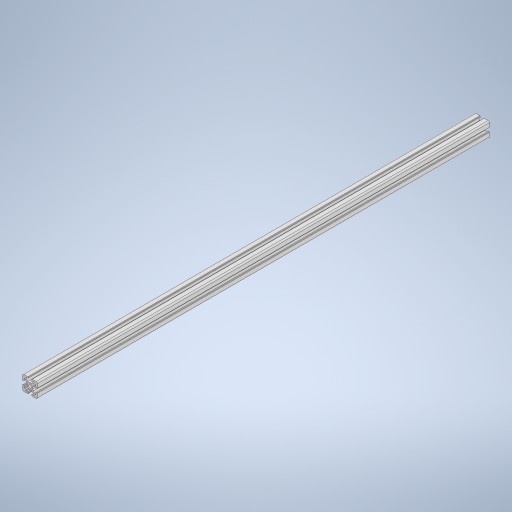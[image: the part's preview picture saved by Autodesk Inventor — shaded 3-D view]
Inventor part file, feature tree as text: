
AUTODESK INVENTOR PART (.ipt)
format: ipt  version: 2023 (Build 270158000, 158)  size: 324,608 bytes
history: mixed  units: in
note: dims shown in document units (in); Inventor stores cm internally (conversion verified against a paired STEP export)
features: mirror x1, imported_body x1
ambient origin geometry x8: Origin, YZ Plane, XZ Plane, XY Plane, X Axis, Y Axis, Z Axis, Center Point
bodies: Solid1 (imported_parasolid)
feature tree (2):
  mirror  "Mirror2"
  imported_body  NMx_Import_Brep_tag  [imported B-rep: ~75 faces, bbox_mm=[20.0, 20.0, 609.6]]
